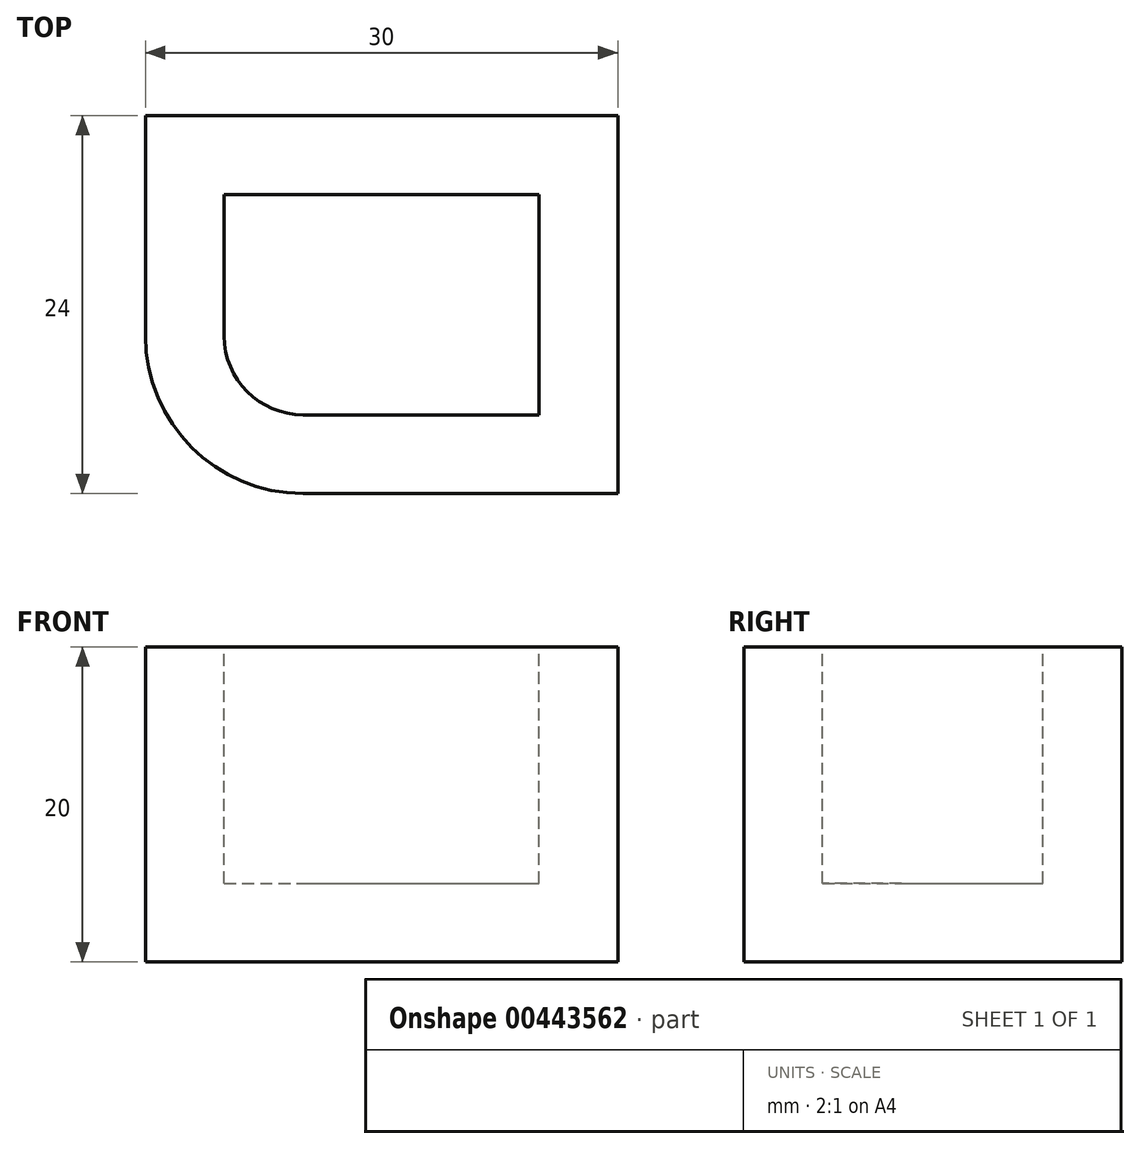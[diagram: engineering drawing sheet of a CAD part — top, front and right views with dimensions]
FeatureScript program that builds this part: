
annotation { "Feature Type Name" : "Feature", "Feature Type Description" : "" }
export const myFeature = defineFeature(function(context is Context, id is Id, definition is map)
    precondition{}
    {
        {
            var Q0;
            Q0=qCreatedBy(makeId("Front.planeOp"),FACE);
            var sketch = newSketch(context, id + "F0", { "sketchPlane" : qUnion([Q0])});
            skLineSegment(sketch, "E0.bottom", {"start": v(0, 0) * mm, "end": v(30, 0) * mm});
            skLineSegment(sketch, "E0.top", {"start": v(0, 20) * mm, "end": v(30, 20) * mm});
            skLineSegment(sketch, "E0.left", {"start": v(0, 0) * mm, "end": v(0, 20) * mm});
            skLineSegment(sketch, "E0.right", {"start": v(30, 0) * mm, "end": v(30, 20) * mm});
            skSolve(sketch);
        }
        {
            var Q0;
            Q0 = qSketchRegion(id + "F0", true);
            extrude(context, id + "F1", {"entities" : qUnion([Q0]), "depth" : 24 * mm});
        }
        {
            var Q0;
            Q0=makeQuery(id+"F1.opExtrude","CAP_EDGE",EDGE,{"disambiguationData":[OSD([sQuery(id+"F0.wireOp",EDGE,"E0.left")])],"isStart":false});
            fillet(context, id + "F2", {"entities" : qUnion([Q0]), "radius" : 10 * mm, "tangentPropagation" : true, "allowEdgeOverflow" : false});
        }
        {
            var Q0;
            Q0=makeQuery(id+"F1.opExtrude","SWEPT_FACE",FACE,{"disambiguationData":[OSD([sQuery(id+"F0.wireOp",EDGE,"E0.top")])]});
            shell(context, id + "F3", {"entities" : qUnion([Q0]), "thickness" : 5 * mm});
        }
    });
